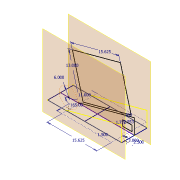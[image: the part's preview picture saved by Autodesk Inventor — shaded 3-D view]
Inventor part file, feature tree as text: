
AUTODESK INVENTOR PART (.ipt)
format: ipt  version: 2019.4 (Build 234330000, 330)  size: 94,208 bytes
history: native  units: in
note: dims shown in document units (in); Inventor stores cm internally (conversion verified against a paired STEP export)
features: sketch x4, plane x2
ambient origin geometry x8: Origin, YZ Plane, XZ Plane, XY Plane, X Axis, Y Axis, Z Axis, Center Point
feature tree (6):
  sketch  "Sketch1"  dims[d9=6.0in]
  sketch  "Sketch2"  dims[d10=2.5in]
  plane  "Work Plane1"
  sketch  "Sketch8"  dims[d11=3.0in]
  plane  "Work Plane4"
  sketch  "Sketch9"  dims[d13=15.625in d14=11.0in d17=15.625in d18=13.0in d19=15.0deg d20=2.9528in d21=1.7717in d22=0.5in d24=1.5in d25=0.0in]
